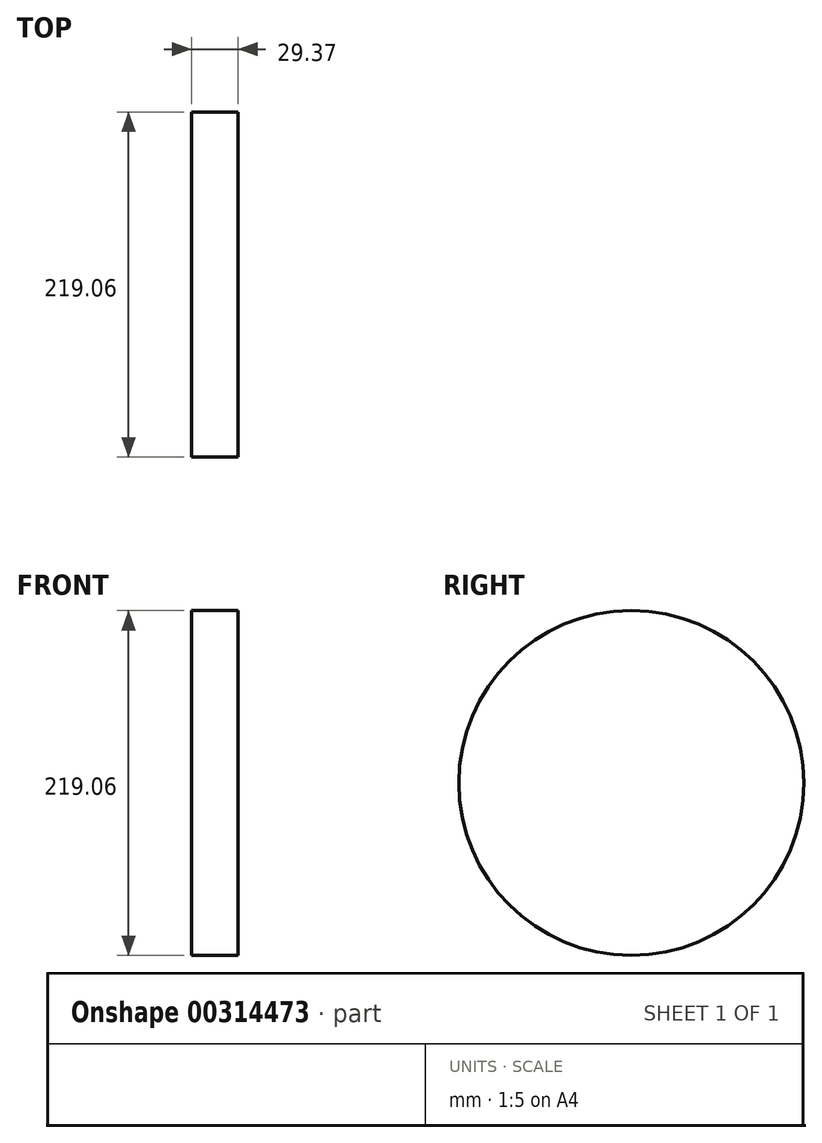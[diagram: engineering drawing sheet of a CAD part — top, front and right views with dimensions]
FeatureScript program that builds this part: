
annotation { "Feature Type Name" : "Feature", "Feature Type Description" : "" }
export const myFeature = defineFeature(function(context is Context, id is Id, definition is map)
    precondition{}
    {
        {
            var Q0;
            Q0=qCreatedBy(makeId("Right.planeOp"),FACE);
            var sketch = newSketch(context, id + "F0", { "sketchPlane" : qUnion([Q0])});
            skCircle(sketch, "E0", {"center": v(0, 0) * mm, "radius": 109.53 * mm});
            skSolve(sketch);
        }
        {
            var Q0;
            Q0 = qSketchRegion(id + "F0", true);
            extrude(context, id + "F1", {"entities" : qUnion([Q0]), "depth" : 12.21 * mm});
        }
        {
            var Q0;
            Q0=makeQuery(id+"F1.opExtrude","CAP_FACE",FACE,{"disambiguationData":[OSD([sQuery(id+"F0.wireOp",EDGE,"E0")])],"isStart":true});
            extrude(context, id + "F2", {"entities" : qUnion([Q0]), "operationType" : NewBodyOperationType.ADD, "depth" : 17.16 * mm});
        }
    });
